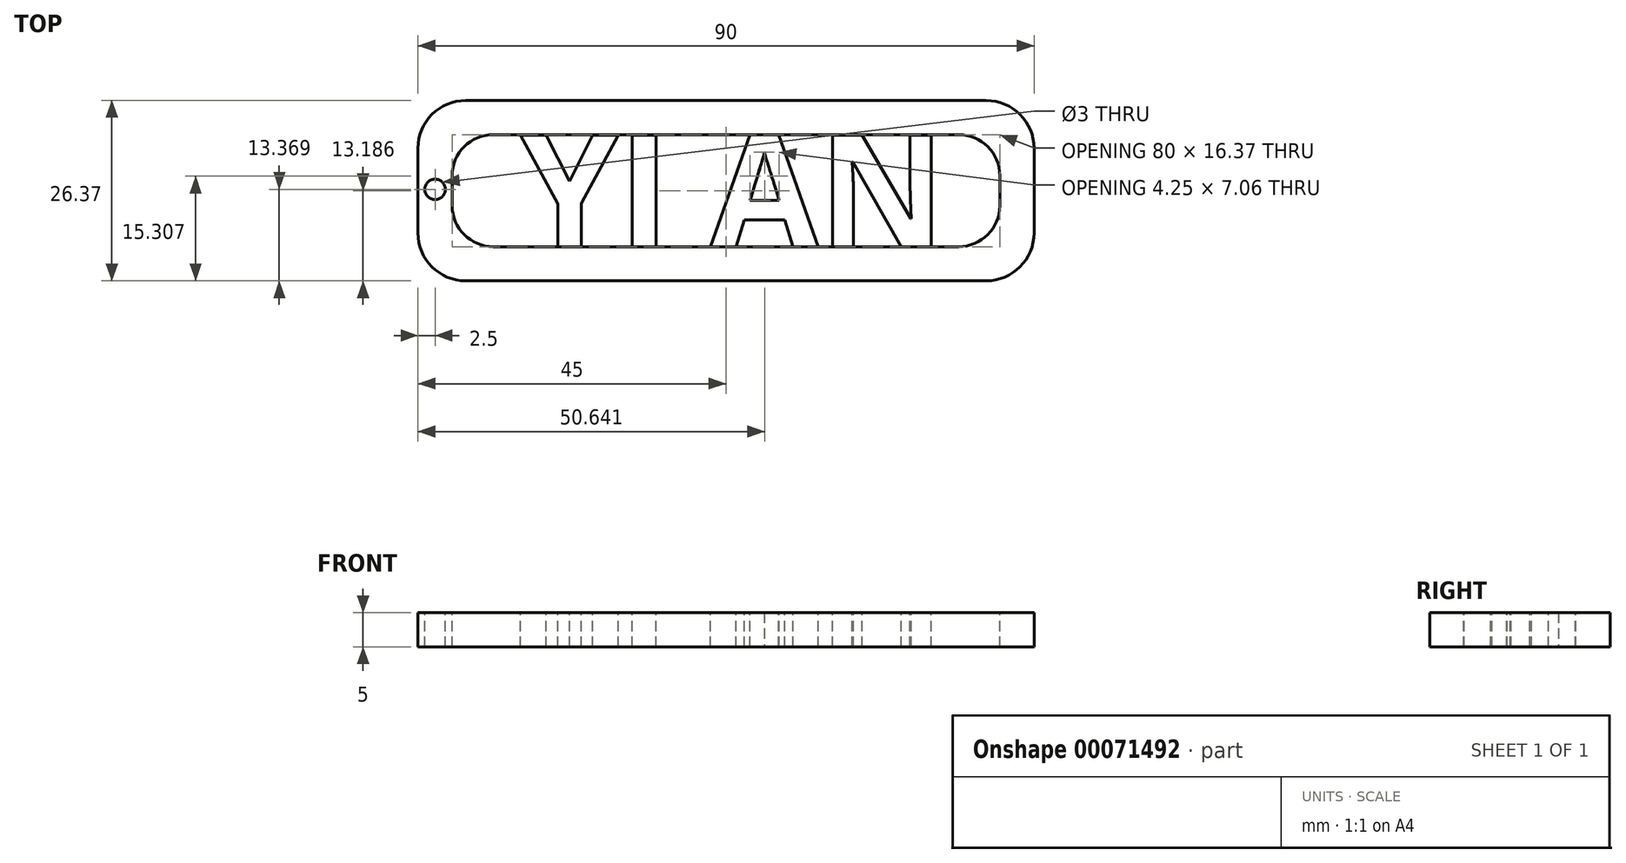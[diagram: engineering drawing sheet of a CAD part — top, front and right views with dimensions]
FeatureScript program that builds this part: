
annotation { "Feature Type Name" : "Feature", "Feature Type Description" : "" }
export const myFeature = defineFeature(function(context is Context, id is Id, definition is map)
    precondition{}
    {
        {
            var Q0;
            Q0=qCreatedBy(makeId("Top.planeOp"),FACE);
            var sketch = newSketch(context, id + "F0", { "sketchPlane" : qUnion([Q0])});
            skText(sketch, "E0", { "text": "YI AN", "fontName": "OpenSans-Bold.ttf"});
            const initialGuessF0  = {"E0": [0, -0.01644, 1, 0, 0.01644]};
            skSetInitialGuess(sketch, initialGuessF0);
            skSolve(sketch);
        }
        {
            var Q0;
            Q0=qSketchRegion(id+"F0",true);
            extrude(context, id + "F1", {"entities" : qUnion([Q0]), "oppositeDirection" : true, "depth" : 5 * mm});
        }
        {
            var Q0;
            Q0=qCreatedBy(makeId("Top.planeOp"),FACE);
            var sketch = newSketch(context, id + "F2", { "sketchPlane" : qUnion([Q0])});
            skLineSegment(sketch, "E1.bottom", {"start": v(-10, -0.07) * mm, "end": v(70, -0.07) * mm});
            skLineSegment(sketch, "E1.top", {"start": v(-10, -16.44) * mm, "end": v(70, -16.44) * mm});
            skLineSegment(sketch, "E1.left", {"start": v(-10, -0.07) * mm, "end": v(-10, -16.44) * mm});
            skLineSegment(sketch, "E1.right", {"start": v(70, -0.07) * mm, "end": v(70, -16.44) * mm});
            skLineSegment(sketch, "E2.bottom", {"start": v(-15, 4.93) * mm, "end": v(75, 4.93) * mm});
            skLineSegment(sketch, "E2.top", {"start": v(-15, -21.44) * mm, "end": v(75, -21.44) * mm});
            skLineSegment(sketch, "E2.left", {"start": v(-15, 4.93) * mm, "end": v(-15, -21.44) * mm});
            skLineSegment(sketch, "E2.right", {"start": v(75, 4.93) * mm, "end": v(75, -21.44) * mm});
            skSolve(sketch);
        }
        {
            var Q0;
            Q0 = qSketchRegion(id + "F2", true);
            extrude(context, id + "F3", {"entities" : qUnion([Q0]), "oppositeDirection" : true, "depth" : 5 * mm});
        }
        {
            var Q0;
            Q0=makeQuery(id+"FkBw86QbWfOq9Hf_5.opExtrude","SWEPT_EDGE",EDGE,{"disambiguationData":[OSD([sQuery(id+"FkUuN3Ar545tSJ0_5.wireOp",EDGE,"50b06f94-d8b9-4e14-ae18-1194ae3a737d.bottom"),sQuery(id+"FkUuN3Ar545tSJ0_5.wireOp",EDGE,"50b06f94-d8b9-4e14-ae18-1194ae3a737d.left")])]});
            var Q1;
            Q1=makeQuery(id+"FkBw86QbWfOq9Hf_5.opExtrude","SWEPT_EDGE",EDGE,{"disambiguationData":[OSD([sQuery(id+"FkUuN3Ar545tSJ0_5.wireOp",EDGE,"50b06f94-d8b9-4e14-ae18-1194ae3a737d.top"),sQuery(id+"FkUuN3Ar545tSJ0_5.wireOp",EDGE,"50b06f94-d8b9-4e14-ae18-1194ae3a737d.left")])]});
            var Q2;
            Q2=makeQuery(id+"FkBw86QbWfOq9Hf_5.opExtrude","SWEPT_EDGE",EDGE,{"disambiguationData":[OSD([sQuery(id+"FkUuN3Ar545tSJ0_5.wireOp",EDGE,"50b06f94-d8b9-4e14-ae18-1194ae3a737d.top"),sQuery(id+"FkUuN3Ar545tSJ0_5.wireOp",EDGE,"50b06f94-d8b9-4e14-ae18-1194ae3a737d.right")])]});
            var Q3;
            Q3=makeQuery(id+"FkBw86QbWfOq9Hf_5.opExtrude","SWEPT_EDGE",EDGE,{"disambiguationData":[OSD([sQuery(id+"FkUuN3Ar545tSJ0_5.wireOp",EDGE,"50b06f94-d8b9-4e14-ae18-1194ae3a737d.bottom"),sQuery(id+"FkUuN3Ar545tSJ0_5.wireOp",EDGE,"50b06f94-d8b9-4e14-ae18-1194ae3a737d.right")])]});
            var Q4;
            Q4=makeQuery(id+"F3.opExtrude","SWEPT_EDGE",EDGE,{"disambiguationData":[OSD([sQuery(id+"F2.wireOp",EDGE,"E2.bottom"),sQuery(id+"F2.wireOp",EDGE,"E2.left")])]});
            var Q5;
            Q5=makeQuery(id+"F3.opExtrude","SWEPT_EDGE",EDGE,{"disambiguationData":[OSD([sQuery(id+"F2.wireOp",EDGE,"E2.top"),sQuery(id+"F2.wireOp",EDGE,"E2.left")])]});
            var Q6;
            Q6=makeQuery(id+"F3.opExtrude","SWEPT_EDGE",EDGE,{"disambiguationData":[OSD([sQuery(id+"F2.wireOp",EDGE,"E2.bottom"),sQuery(id+"F2.wireOp",EDGE,"E2.right")])]});
            var Q7;
            Q7=makeQuery(id+"F3.opExtrude","SWEPT_EDGE",EDGE,{"disambiguationData":[OSD([sQuery(id+"F2.wireOp",EDGE,"E2.top"),sQuery(id+"F2.wireOp",EDGE,"E2.right")])]});
            fillet(context, id + "F4", {"entities" : qUnion([Q0, Q1, Q2, Q3, Q4, Q5, Q6, Q7]), "radius" : 7 * mm, "tangentPropagation" : true, "allowEdgeOverflow" : false});
        }
        {
            var Q0;
            Q0=makeQuery(id+"FkBw86QbWfOq9Hf_5.opExtrude","SWEPT_EDGE",EDGE,{"disambiguationData":[OSD([sQuery(id+"FkUuN3Ar545tSJ0_5.wireOp",EDGE,"9ad2f146-a91b-4102-ac88-bf789ada3a88.bottom"),sQuery(id+"FkUuN3Ar545tSJ0_5.wireOp",EDGE,"9ad2f146-a91b-4102-ac88-bf789ada3a88.right")])]});
            var Q1;
            Q1=makeQuery(id+"FkBw86QbWfOq9Hf_5.opExtrude","SWEPT_EDGE",EDGE,{"disambiguationData":[OSD([sQuery(id+"FkUuN3Ar545tSJ0_5.wireOp",EDGE,"9ad2f146-a91b-4102-ac88-bf789ada3a88.top"),sQuery(id+"FkUuN3Ar545tSJ0_5.wireOp",EDGE,"9ad2f146-a91b-4102-ac88-bf789ada3a88.right")])]});
            var Q2;
            Q2=makeQuery(id+"FkBw86QbWfOq9Hf_5.opExtrude","SWEPT_EDGE",EDGE,{"disambiguationData":[OSD([sQuery(id+"FkUuN3Ar545tSJ0_5.wireOp",EDGE,"9ad2f146-a91b-4102-ac88-bf789ada3a88.bottom"),sQuery(id+"FkUuN3Ar545tSJ0_5.wireOp",EDGE,"9ad2f146-a91b-4102-ac88-bf789ada3a88.left")])]});
            var Q3;
            Q3=makeQuery(id+"FkBw86QbWfOq9Hf_5.opExtrude","SWEPT_EDGE",EDGE,{"disambiguationData":[OSD([sQuery(id+"FkUuN3Ar545tSJ0_5.wireOp",EDGE,"9ad2f146-a91b-4102-ac88-bf789ada3a88.top"),sQuery(id+"FkUuN3Ar545tSJ0_5.wireOp",EDGE,"9ad2f146-a91b-4102-ac88-bf789ada3a88.left")])]});
            var Q4;
            Q4=makeQuery(id+"F3.opExtrude","SWEPT_EDGE",EDGE,{"disambiguationData":[OSD([sQuery(id+"F2.wireOp",EDGE,"E1.bottom"),sQuery(id+"F2.wireOp",EDGE,"E1.left")])]});
            var Q5;
            Q5=makeQuery(id+"F3.opExtrude","SWEPT_EDGE",EDGE,{"disambiguationData":[OSD([sQuery(id+"F2.wireOp",EDGE,"E1.top"),sQuery(id+"F2.wireOp",EDGE,"E1.left")])]});
            var Q6;
            Q6=makeQuery(id+"F3.opExtrude","SWEPT_EDGE",EDGE,{"disambiguationData":[OSD([sQuery(id+"F2.wireOp",EDGE,"E1.bottom"),sQuery(id+"F2.wireOp",EDGE,"E1.right")])]});
            var Q7;
            Q7=makeQuery(id+"F3.opExtrude","SWEPT_EDGE",EDGE,{"disambiguationData":[OSD([sQuery(id+"F2.wireOp",EDGE,"E1.top"),sQuery(id+"F2.wireOp",EDGE,"E1.right")])]});
            fillet(context, id + "F5", {"entities" : qUnion([Q0, Q1, Q2, Q3, Q4, Q5, Q6, Q7]), "radius" : 6 * mm, "tangentPropagation" : true, "allowEdgeOverflow" : false});
        }
        {
            var Q0;
            Q0=makeQuery(id+"F3.opExtrude","CAP_FACE",FACE,{"disambiguationData":[OSD([sQuery(id+"F2.wireOp",EDGE,"E1.bottom"),sQuery(id+"F2.wireOp",EDGE,"E1.top"),sQuery(id+"F2.wireOp",EDGE,"E1.left"),sQuery(id+"F2.wireOp",EDGE,"E1.right"),sQuery(id+"F2.wireOp",EDGE,"E2.bottom"),sQuery(id+"F2.wireOp",EDGE,"E2.top"),sQuery(id+"F2.wireOp",EDGE,"E2.left"),sQuery(id+"F2.wireOp",EDGE,"E2.right")])],"isStart":true});
            var sketch = newSketch(context, id + "F6", { "sketchPlane" : qUnion([Q0])});
            skCircle(sketch, "E3", {"center": v(-12.5, -8.07) * mm, "radius": 1.5 * mm});
            skSolve(sketch);
        }
        {
            var Q0;
            Q0 = qSketchRegion(id + "F6", true);
            extrude(context, id + "F7", {"entities" : qUnion([Q0]), "operationType" : NewBodyOperationType.REMOVE, "endBound" : BoundingType.THROUGH_ALL, "oppositeDirection" : true, "depth" : 25 * mm});
        }
    });
